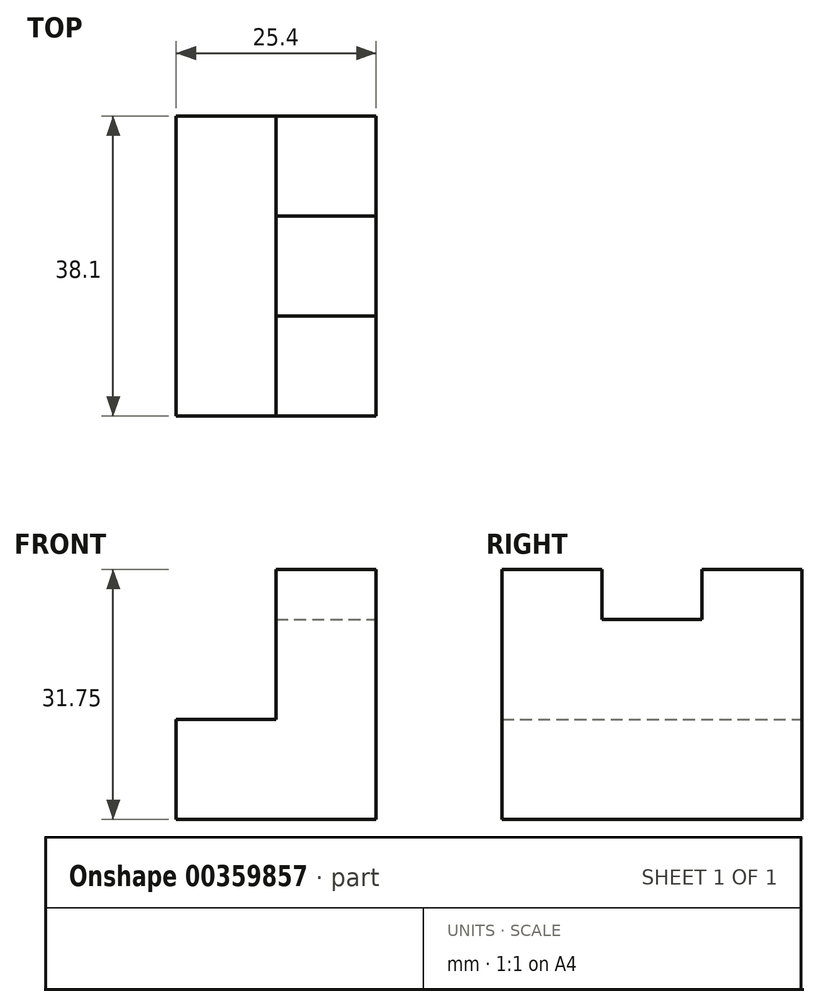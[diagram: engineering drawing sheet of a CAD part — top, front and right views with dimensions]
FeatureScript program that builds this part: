
annotation { "Feature Type Name" : "Feature", "Feature Type Description" : "" }
export const myFeature = defineFeature(function(context is Context, id is Id, definition is map)
    precondition{}
    {
        {
            var Q0;
            Q0=qCreatedBy(makeId("Front.planeOp"),FACE);
            var sketch = newSketch(context, id + "F0", { "sketchPlane" : qUnion([Q0])});
            skLineSegment(sketch, "E0", {"start": v(0, 0) * mm, "end": v(25.4, 0) * mm});
            skLineSegment(sketch, "E1", {"start": v(25.4, 0) * mm, "end": v(25.4, 31.75) * mm});
            skLineSegment(sketch, "E2", {"start": v(25.4, 31.75) * mm, "end": v(12.7, 31.75) * mm});
            skLineSegment(sketch, "E3", {"start": v(12.7, 31.75) * mm, "end": v(12.7, 12.7) * mm});
            skLineSegment(sketch, "E4", {"start": v(12.7, 12.7) * mm, "end": v(0, 12.7) * mm});
            skLineSegment(sketch, "E5", {"start": v(0, 12.7) * mm, "end": v(0, 0) * mm});
            skSolve(sketch);
        }
        {
            var Q0;
            Q0 = qSketchRegion(id + "F0", true);
            extrude(context, id + "F1", {"entities" : qUnion([Q0]), "depth" : 38.1 * mm});
        }
        {
            var Q0;
            Q0=makeQuery(id+"F1.opExtrude","SWEPT_FACE",FACE,{"disambiguationData":[OSD([sQuery(id+"F0.wireOp",EDGE,"E2")])]});
            var sketch = newSketch(context, id + "F2", { "sketchPlane" : qUnion([Q0])});
            skLineSegment(sketch, "E6", {"start": v(0, 0) * mm, "end": v(0, -16.56) * mm});
            skLineSegment(sketch, "E7", {"start": v(25.4, -16.56) * mm, "end": v(25.4, 0) * mm});
            skLineSegment(sketch, "E8", {"start": v(25.4, 0) * mm, "end": v(0, 0) * mm});
            skLineSegment(sketch, "E9", {"start": v(12.7, -12.7) * mm, "end": v(25.4, -12.7) * mm});
            skLineSegment(sketch, "E10", {"start": v(25.4, -12.7) * mm, "end": v(25.4, -25.4) * mm});
            skLineSegment(sketch, "E11", {"start": v(25.4, -25.4) * mm, "end": v(12.7, -25.4) * mm});
            skLineSegment(sketch, "E12", {"start": v(12.7, -25.4) * mm, "end": v(12.7, -12.7) * mm});
            skSolve(sketch);
        }
        {
            var Q0;
            {var subQ0=sQuery(id+"F2.wireOp",EDGE,"E9");Q0=makeQuery(id+"F2.imprint","IMPRINT",FACE,{"disambiguationData":[TD([[makeQuery(id+"F2.imprint","IMPRINT",EDGE,{"derivedFrom":subQ0}),-1.0]])]});}
            extrude(context, id + "F3", {"entities" : qUnion([Q0]), "operationType" : NewBodyOperationType.REMOVE, "oppositeDirection" : true, "depth" : 6.35 * mm});
        }
    });
